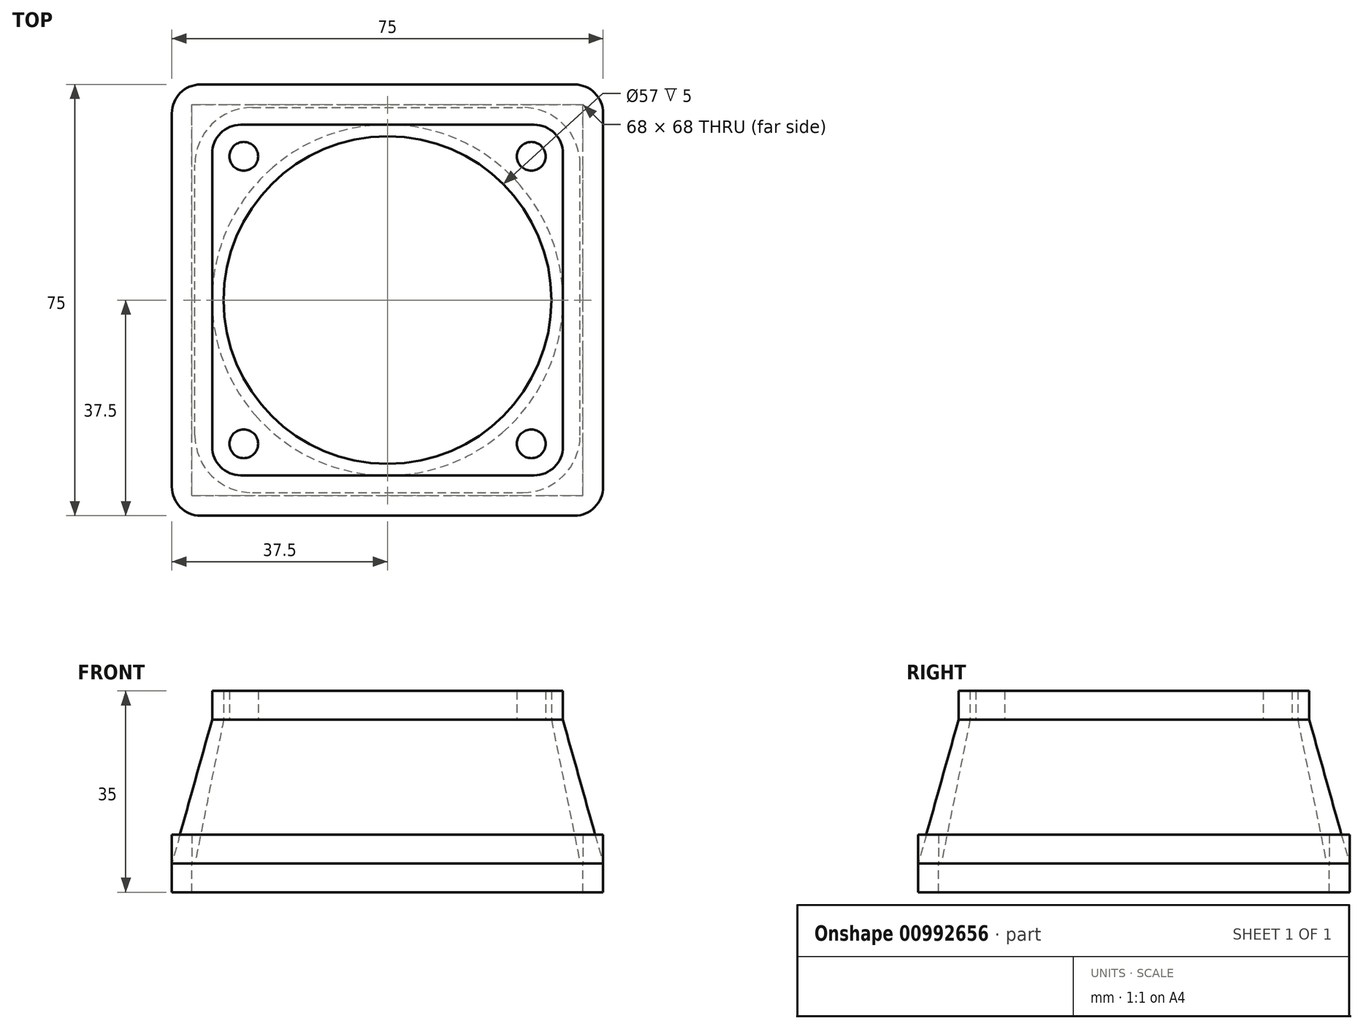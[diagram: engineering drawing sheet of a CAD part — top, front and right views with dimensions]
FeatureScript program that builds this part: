
annotation { "Feature Type Name" : "Feature", "Feature Type Description" : "" }
export const myFeature = defineFeature(function(context is Context, id is Id, definition is map)
    precondition{}
    {
        {
            var Q0;
            Q0=qCreatedBy(makeId("Top.planeOp"),FACE);
            cPlane(context, id + "F0", {"entities" : qUnion([Q0]), "cplaneType" : CPlaneType.OFFSET, "offset" : 25 * mm, "oppositeDirection" : true, "width" : 150 * mm, "height" : 150 * mm});
        }
        {
            var Q0;
            Q0=qCreatedBy(makeId("Top.planeOp"),FACE);
            var sketch = newSketch(context, id + "F1", { "sketchPlane" : qUnion([Q0])});
            skLineSegment(sketch, "E0.bottom", {"start": v(25.5, -30.5) * mm, "end": v(-25.5, -30.5) * mm});
            skLineSegment(sketch, "E0.top", {"start": v(25.5, 30.5) * mm, "end": v(-25.5, 30.5) * mm});
            skLineSegment(sketch, "E0.left", {"start": v(30.5, -25.5) * mm, "end": v(30.5, 25.5) * mm});
            skLineSegment(sketch, "E0.right", {"start": v(-30.5, -25.5) * mm, "end": v(-30.5, 25.5) * mm});
            skPoint(sketch, "E0.middle", {"position": v(0, 0) * mm});
            skPoint(sketch, "E1.visualSharp", {"position": v(30.5, -30.5) * mm});
            skArc(sketch, "E1.filletArc", {"start": v(25.5, -30.5) * mm, "mid": v(29.04, -29.04) * mm, "end": v(30.5, -25.5) * mm});
            skPoint(sketch, "E2.visualSharp", {"position": v(30.5, 30.5) * mm});
            skArc(sketch, "E2.filletArc", {"start": v(30.5, 25.5) * mm, "mid": v(29.04, 29.04) * mm, "end": v(25.5, 30.5) * mm});
            skPoint(sketch, "E3.visualSharp", {"position": v(-30.5, 30.5) * mm});
            skArc(sketch, "E3.filletArc", {"start": v(-25.5, 30.5) * mm, "mid": v(-29.04, 29.04) * mm, "end": v(-30.5, 25.5) * mm});
            skPoint(sketch, "E4.visualSharp", {"position": v(-30.5, -30.5) * mm});
            skArc(sketch, "E4.filletArc", {"start": v(-30.5, -25.5) * mm, "mid": v(-29.04, -29.04) * mm, "end": v(-25.5, -30.5) * mm});
            skSolve(sketch);
        }
        {
            var Q0;
            Q0=qCreatedBy(id+"F0.planeOp",FACE);
            var sketch = newSketch(context, id + "F2", { "sketchPlane" : qUnion([Q0])});
            skLineSegment(sketch, "E5.bottom", {"start": v(-23.5, -33.5) * mm, "end": v(23.5, -33.5) * mm});
            skLineSegment(sketch, "E5.top", {"start": v(-23.5, 33.5) * mm, "end": v(23.5, 33.5) * mm});
            skLineSegment(sketch, "E5.left", {"start": v(-33.5, -23.5) * mm, "end": v(-33.5, 23.5) * mm});
            skLineSegment(sketch, "E5.right", {"start": v(33.5, -23.5) * mm, "end": v(33.5, 23.5) * mm});
            skPoint(sketch, "E5.middle", {"position": v(0, 0) * mm});
            skPoint(sketch, "E6.visualSharp", {"position": v(-33.5, 33.5) * mm});
            skArc(sketch, "E6.filletArc", {"start": v(-23.5, 33.5) * mm, "mid": v(-30.57, 30.57) * mm, "end": v(-33.5, 23.5) * mm});
            skPoint(sketch, "E7.visualSharp", {"position": v(33.5, 33.5) * mm});
            skArc(sketch, "E7.filletArc", {"start": v(33.5, 23.5) * mm, "mid": v(30.57, 30.57) * mm, "end": v(23.5, 33.5) * mm});
            skPoint(sketch, "E8.visualSharp", {"position": v(33.5, -33.5) * mm});
            skArc(sketch, "E8.filletArc", {"start": v(23.5, -33.5) * mm, "mid": v(30.57, -30.57) * mm, "end": v(33.5, -23.5) * mm});
            skPoint(sketch, "E9.visualSharp", {"position": v(-33.5, -33.5) * mm});
            skArc(sketch, "E9.filletArc", {"start": v(-33.5, -23.5) * mm, "mid": v(-30.57, -30.57) * mm, "end": v(-23.5, -33.5) * mm});
            skSolve(sketch);
        }
        {
            var Q0;
            Q0=qCreatedBy(makeId("Top.planeOp"),FACE);
            var sketch = newSketch(context, id + "F3", { "sketchPlane" : qUnion([Q0])});
            skCircle(sketch, "E10", {"center": v(0, 0) * mm, "radius": 28.5 * mm});
            skSolve(sketch);
        }
        {
            var Q0;
            Q0=qCreatedBy(id+"F0.planeOp",FACE);
            var sketch = newSketch(context, id + "F4", { "sketchPlane" : qUnion([Q0])});
            skLineSegment(sketch, "E11.bottom", {"start": v(32.5, -37.5) * mm, "end": v(-32.5, -37.5) * mm});
            skLineSegment(sketch, "E11.top", {"start": v(32.5, 37.5) * mm, "end": v(-32.5, 37.5) * mm});
            skLineSegment(sketch, "E11.left", {"start": v(37.5, -32.5) * mm, "end": v(37.5, 32.5) * mm});
            skLineSegment(sketch, "E11.right", {"start": v(-37.5, -32.5) * mm, "end": v(-37.5, 32.5) * mm});
            skPoint(sketch, "E11.middle", {"position": v(0, 0) * mm});
            skPoint(sketch, "E12.visualSharp", {"position": v(37.5, -37.5) * mm});
            skArc(sketch, "E12.filletArc", {"start": v(32.5, -37.5) * mm, "mid": v(36.04, -36.04) * mm, "end": v(37.5, -32.5) * mm});
            skPoint(sketch, "E13.visualSharp", {"position": v(37.5, 37.5) * mm});
            skArc(sketch, "E13.filletArc", {"start": v(37.5, 32.5) * mm, "mid": v(36.04, 36.04) * mm, "end": v(32.5, 37.5) * mm});
            skPoint(sketch, "E14.visualSharp", {"position": v(-37.5, 37.5) * mm});
            skArc(sketch, "E14.filletArc", {"start": v(-32.5, 37.5) * mm, "mid": v(-36.04, 36.04) * mm, "end": v(-37.5, 32.5) * mm});
            skPoint(sketch, "E15.visualSharp", {"position": v(-37.5, -37.5) * mm});
            skArc(sketch, "E15.filletArc", {"start": v(-37.5, -32.5) * mm, "mid": v(-36.04, -36.04) * mm, "end": v(-32.5, -37.5) * mm});
            skSolve(sketch);
        }
        {
            var Q0;
            Q0=qCreatedBy(makeId("Top.planeOp"),FACE);
            var sketch = newSketch(context, id + "F5", { "sketchPlane" : qUnion([Q0])});
            skCircle(sketch, "E16", {"center": v(0, 0) * mm, "radius": 30.5 * mm});
            skSolve(sketch);
        }
        {
            var Q0;
            Q0=qCreatedBy(id+"F0.planeOp",FACE);
            var sketch = newSketch(context, id + "F6", { "sketchPlane" : qUnion([Q0])});
            skLineSegment(sketch, "E17.bottom", {"start": v(-34, -34) * mm, "end": v(34, -34) * mm});
            skLineSegment(sketch, "E17.top", {"start": v(-34, 34) * mm, "end": v(34, 34) * mm});
            skLineSegment(sketch, "E17.left", {"start": v(-34, -34) * mm, "end": v(-34, 34) * mm});
            skLineSegment(sketch, "E17.right", {"start": v(34, -34) * mm, "end": v(34, 34) * mm});
            skPoint(sketch, "E17.middle", {"position": v(0, 0) * mm});
            skSolve(sketch);
        }
        {
            var Q0;
            Q0=qSketchRegion(id+"F9",true);
            var Q1;
            Q1=qSketchRegion(id+"F1",true);
            extrude(context, id + "F7", {"entities" : qUnion([Q0, Q1]), "depth" : 5 * mm, "offsetDistance" : 25 * mm});
        }
        {
            var Q0;
            Q0=qCreatedBy(makeId("Top.planeOp"),FACE);
            var sketch = newSketch(context, id + "F8", { "sketchPlane" : qUnion([Q0])});
            skLineSegment(sketch, "E18.bottom", {"start": v(-25, 25) * mm, "end": v(25, 25) * mm, "construction": true});
            skLineSegment(sketch, "E18.top", {"start": v(-25, -25) * mm, "end": v(25, -25) * mm, "construction": true});
            skLineSegment(sketch, "E18.left", {"start": v(-25, 25) * mm, "end": v(-25, -25) * mm, "construction": true});
            skLineSegment(sketch, "E18.right", {"start": v(25, 25) * mm, "end": v(25, -25) * mm, "construction": true});
            skPoint(sketch, "E18.middle", {"position": v(0, 0) * mm});
            skSolve(sketch);
        }
        {
            var Q0;
            Q0=qCreatedBy(makeId("Top.planeOp"),FACE);
            var sketch = newSketch(context, id + "F9", { "sketchPlane" : qUnion([Q0])});
            skCircle(sketch, "E19", {"center": v(-25, 25) * mm, "radius": 2.5 * mm});
            skCircle(sketch, "E20", {"center": v(25, 25) * mm, "radius": 2.5 * mm});
            skCircle(sketch, "E21", {"center": v(25, -25) * mm, "radius": 2.5 * mm});
            skCircle(sketch, "E22", {"center": v(-25, -25) * mm, "radius": 2.5 * mm});
            skSolve(sketch);
        }
        {
            var Q0;
            Q0=qSketchRegion(id+"F3",true);
            var Q1;
            Q1=qSketchRegion(id+"F6",true);
            var Q2;
            Q2=qSketchRegion(id+"F4",true);
            extrude(context, id + "F10", {"entities" : qUnion([Q0, Q1, Q2]), "depth" : 5 * mm, "offsetDistance" : 25 * mm});
        }
        {
            var Q0;
            Q0=qSketchRegion(id+"F9",true);
            extrude(context, id + "F11", {"entities" : qUnion([Q0]), "depth" : 5 * mm, "offsetDistance" : 25 * mm});
        }
        {
            var Q0;
            Q0=makeQuery(id+"F10.opExtrude","SWEPT_BODY",BODY,{"disambiguationData":[OSD([sQuery(id+"F3.wireOp",EDGE,"E10")])]});
            var Q1;
            Q1=makeQuery(id+"F11.opExtrude","SWEPT_BODY",BODY,{"disambiguationData":[OSD([sQuery(id+"F9.wireOp",EDGE,"E20")])]});
            var Q2;
            Q2=makeQuery(id+"F11.opExtrude","SWEPT_BODY",BODY,{"disambiguationData":[OSD([sQuery(id+"F9.wireOp",EDGE,"E22")])]});
            var Q3;
            Q3=makeQuery(id+"F11.opExtrude","SWEPT_BODY",BODY,{"disambiguationData":[OSD([sQuery(id+"F9.wireOp",EDGE,"E19")])]});
            var Q4;
            Q4=makeQuery(id+"F11.opExtrude","SWEPT_BODY",BODY,{"disambiguationData":[OSD([sQuery(id+"F9.wireOp",EDGE,"E21")])]});
            var Q5;
            Q5=makeQuery(id+"F7.opExtrude","SWEPT_BODY",BODY,{"disambiguationData":[OSD([sQuery(id+"F1.wireOp",EDGE,"E0.bottom"),sQuery(id+"F1.wireOp",EDGE,"E0.top"),sQuery(id+"F1.wireOp",EDGE,"E0.left"),sQuery(id+"F1.wireOp",EDGE,"E0.right"),sQuery(id+"F1.wireOp",EDGE,"E1.filletArc"),sQuery(id+"F1.wireOp",EDGE,"E2.filletArc"),sQuery(id+"F1.wireOp",EDGE,"E3.filletArc"),sQuery(id+"F1.wireOp",EDGE,"E4.filletArc")])]});
            booleanBodies(context, id + "F12", {"operationType" : BooleanOperationType.SUBTRACTION, "tools" : qUnion([Q0, Q1, Q2, Q3, Q4]), "targets" : qUnion([Q5])});
        }
        {
            var Q0;
            Q0=qSketchRegion(id+"F3",true);
            var Q1;
            Q1=qSketchRegion(id+"F2",true);
            loft(context, id + "F13", {"sheetProfilesArray" : [{ "sheetProfileEntities" : qUnion([Q0]) }, { "sheetProfileEntities" : qUnion([Q1]) }]});
        }
        {
            var Q0;
            Q0=qSketchRegion(id+"F5",true);
            var Q1;
            Q1=qSketchRegion(id+"F4",true);
            loft(context, id + "F14", {"sheetProfilesArray" : [{ "sheetProfileEntities" : qUnion([Q0]) }, { "sheetProfileEntities" : qUnion([Q1]) }]});
        }
        {
            var Q0;
            Q0=makeQuery(id+"F13.opLoft","SWEPT_BODY",BODY,{"disambiguationData":[OSD([makeQuery(id+"F2.imprint","IMPRINT",FACE,{"disambiguationData":[TD([[makeQuery(id+"F2.imprint","IMPRINT",EDGE,{"derivedFrom":sQuery(id+"F2.wireOp",EDGE,"E5.bottom")}),1.0]])]}),makeQuery(id+"F3.imprint","IMPRINT",FACE,{"disambiguationData":[TD([[makeQuery(id+"F3.imprint","IMPRINT",EDGE,{"derivedFrom":sQuery(id+"F3.wireOp",EDGE,"E10")}),1.0]])]})])]});
            var Q1;
            Q1=makeQuery(id+"F14.opLoft","SWEPT_BODY",BODY,{"disambiguationData":[OSD([makeQuery(id+"F4.imprint","IMPRINT",FACE,{"disambiguationData":[TD([[makeQuery(id+"F4.imprint","IMPRINT",EDGE,{"derivedFrom":sQuery(id+"F4.wireOp",EDGE,"E11.bottom")}),-1.0]])]}),makeQuery(id+"F5.imprint","IMPRINT",FACE,{"disambiguationData":[TD([[makeQuery(id+"F5.imprint","IMPRINT",EDGE,{"derivedFrom":sQuery(id+"F5.wireOp",EDGE,"E16")}),1.0]])]})])]});
            booleanBodies(context, id + "F15", {"operationType" : BooleanOperationType.SUBTRACTION, "tools" : qUnion([Q0]), "targets" : qUnion([Q1])});
        }
        {
            var Q0;
            Q0=makeQuery(id+"F4.imprint","IMPRINT",FACE,{"disambiguationData":[TD([[makeQuery(id+"F4.imprint","IMPRINT",EDGE,{"derivedFrom":sQuery(id+"F4.wireOp",EDGE,"E11.bottom")}),-1.0]])]});
            extrude(context, id + "F16", {"entities" : qUnion([Q0]), "oppositeDirection" : true, "depth" : 5 * mm, "offsetDistance" : 25 * mm});
        }
        {
            var Q0;
            Q0=qSketchRegion(id+"F6",true);
            extrude(context, id + "F17", {"entities" : qUnion([Q0]), "oppositeDirection" : true, "depth" : 10 * mm, "offsetDistance" : 25 * mm});
        }
        {
            var Q0;
            Q0=makeQuery(id+"F17.opExtrude","SWEPT_BODY",BODY,{"disambiguationData":[OSD([sQuery(id+"F6.wireOp",EDGE,"E17.bottom"),sQuery(id+"F6.wireOp",EDGE,"E17.top"),sQuery(id+"F6.wireOp",EDGE,"E17.left"),sQuery(id+"F6.wireOp",EDGE,"E17.right")])]});
            var Q1;
            Q1=makeQuery(id+"F16.opExtrude","SWEPT_BODY",BODY,{"disambiguationData":[OSD([sQuery(id+"F4.wireOp",EDGE,"E11.bottom"),sQuery(id+"F4.wireOp",EDGE,"E11.top"),sQuery(id+"F4.wireOp",EDGE,"E11.left"),sQuery(id+"F4.wireOp",EDGE,"E11.right"),sQuery(id+"F4.wireOp",EDGE,"E12.filletArc"),sQuery(id+"F4.wireOp",EDGE,"E13.filletArc"),sQuery(id+"F4.wireOp",EDGE,"E14.filletArc"),sQuery(id+"F4.wireOp",EDGE,"E15.filletArc")])]});
            booleanBodies(context, id + "F18", {"operationType" : BooleanOperationType.SUBTRACTION, "tools" : qUnion([Q0]), "targets" : qUnion([Q1])});
        }
    });
